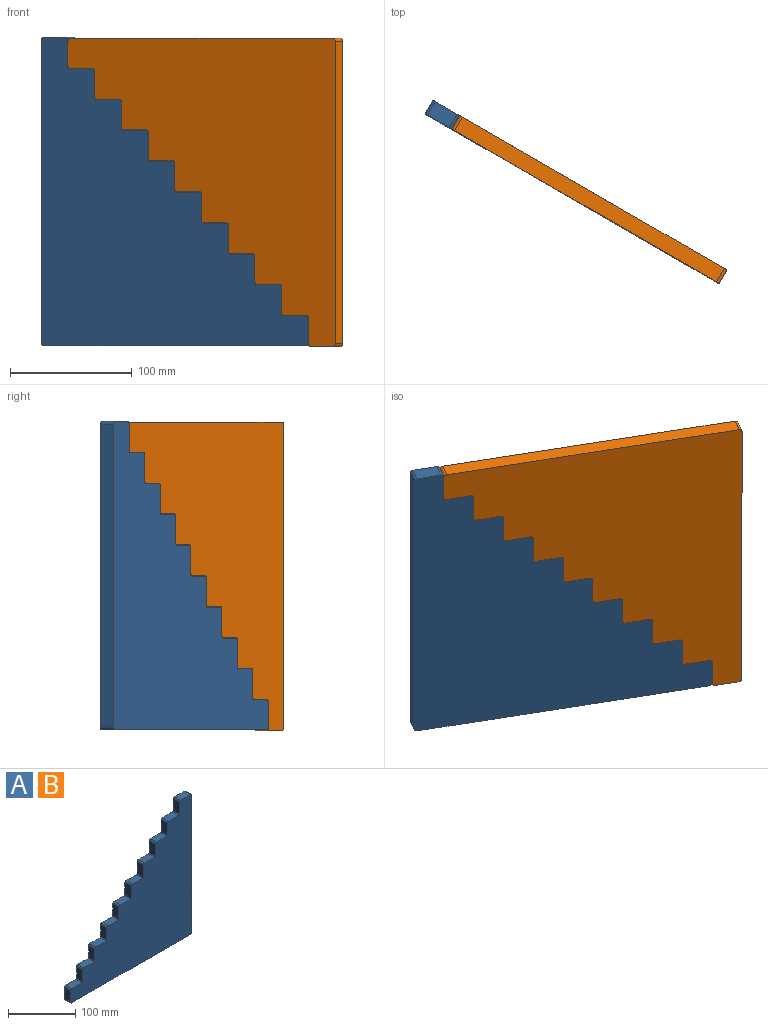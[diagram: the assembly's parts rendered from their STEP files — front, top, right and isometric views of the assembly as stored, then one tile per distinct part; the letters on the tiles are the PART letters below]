
ASSEMBLY  parts=2 mates=4
PART A: 46 faces, bbox 254x12.7x254 mm
  f0: plane 248.92x12.7mm, normal (0,0,-1), area 3161.3mm2, adj f22,f23,f24,f36
  f1: plane 248.92x12.7mm, normal (1,0,0), area 3161.3mm2, adj f22,f23,f24,f25
  f2: plane 20.32x12.7mm, normal (0,0,1), area 258.1mm2, adj f22,f23,f25,f26
  f3: plane 21.59x12.7mm, normal (-1,0,0), area 274.2mm2, adj f22,f23,f26,f37
  f4: plane 21.59x12.7mm, normal (0,0,1), area 274.2mm2, adj f22,f23,f27,f37
  f5: plane 21.59x12.7mm, normal (-1,0,0), area 274.2mm2, adj f22,f23,f27,f38
  f6: plane 21.59x12.7mm, normal (0,0,1), area 274.2mm2, adj f22,f23,f28,f38
  f7: plane 21.59x12.7mm, normal (-1,0,0), area 274.2mm2, adj f22,f23,f28,f39
  f8: plane 21.59x12.7mm, normal (0,0,1), area 274.2mm2, adj f22,f23,f29,f39
  f9: plane 21.59x12.7mm, normal (-1,0,0), area 274.2mm2, adj f22,f23,f29,f40
  f10: plane 21.59x12.7mm, normal (0,0,1), area 274.2mm2, adj f22,f23,f30,f40
  f11: plane 21.59x12.7mm, normal (-1,0,0), area 274.2mm2, adj f22,f23,f30,f41
  f12: plane 21.59x12.7mm, normal (0,0,1), area 274.2mm2, adj f22,f23,f31,f41
  f13: plane 21.59x12.7mm, normal (-1,0,0), area 274.2mm2, adj f22,f23,f31,f42
  f14: plane 21.59x12.7mm, normal (0,0,1), area 274.2mm2, adj f22,f23,f32,f42
  f15: plane 21.59x12.7mm, normal (-1,0,0), area 274.2mm2, adj f22,f23,f32,f43
  f16: plane 21.59x12.7mm, normal (0,0,1), area 274.2mm2, adj f22,f23,f33,f43
  f17: plane 21.59x12.7mm, normal (-1,0,0), area 274.2mm2, adj f22,f23,f33,f44
  f18: plane 21.59x12.7mm, normal (0,0,1), area 274.2mm2, adj f22,f23,f34,f44
  f19: plane 21.59x12.7mm, normal (-1,0,0), area 274.2mm2, adj f22,f23,f34,f45
  f20: plane 21.59x12.7mm, normal (0,0,1), area 274.2mm2, adj f22,f23,f35,f45
  f21: plane 20.32x12.7mm, normal (-1,0,0), area 258.1mm2, adj f22,f23,f35,f36
  f22: plane 254x254mm, normal (0,-1,0), area 35468.9mm2, adj f0,f1,f2,f3,f4,f5,f6,f7
  f23: plane 254x254mm, normal (0,1,0), area 35468.9mm2, adj f0,f1,f2,f3,f4,f5,f6,f7
  f24: cylinder r=2.54mm len=12.7mm, axis (0,-1,0), area 50.7mm2, adj f0,f1,f22,f23
  f25: cylinder r=2.54mm len=12.7mm, axis (0,1,0), area 50.7mm2, adj f1,f2,f22,f23
  f26: cylinder r=2.54mm len=12.7mm, axis (0,-1,0), area 50.7mm2, adj f2,f3,f22,f23
  f27: cylinder r=2.54mm len=12.7mm, axis (0,1,0), area 50.7mm2, adj f4,f5,f22,f23
  f28: cylinder r=2.54mm len=12.7mm, axis (0,1,0), area 50.7mm2, adj f6,f7,f22,f23
  f29: cylinder r=2.54mm len=12.7mm, axis (0,1,0), area 50.7mm2, adj f8,f9,f22,f23
  f30: cylinder r=2.54mm len=12.7mm, axis (0,1,0), area 50.7mm2, adj f10,f11,f22,f23
  f31: cylinder r=2.54mm len=12.7mm, axis (0,1,0), area 50.7mm2, adj f12,f13,f22,f23
  f32: cylinder r=2.54mm len=12.7mm, axis (0,1,0), area 50.7mm2, adj f14,f15,f22,f23
  f33: cylinder r=2.54mm len=12.7mm, axis (0,1,0), area 50.7mm2, adj f16,f17,f22,f23
  f34: cylinder r=2.54mm len=12.7mm, axis (0,1,0), area 50.7mm2, adj f18,f19,f22,f23
  f35: cylinder r=2.54mm len=12.7mm, axis (0,1,0), area 50.7mm2, adj f20,f21,f22,f23
  f36: cylinder r=2.54mm len=12.7mm, axis (0,1,0), area 50.7mm2, adj f0,f21,f22,f23
  f37: cylinder r=1.27mm len=12.7mm, axis (0,-1,0), area 25.3mm2, adj f3,f4,f22,f23
  f38: cylinder r=1.27mm len=12.7mm, axis (0,-1,0), area 25.3mm2, adj f5,f6,f22,f23
  f39: cylinder r=1.27mm len=12.7mm, axis (0,-1,0), area 25.3mm2, adj f7,f8,f22,f23
  f40: cylinder r=1.27mm len=12.7mm, axis (0,-1,0), area 25.3mm2, adj f9,f10,f22,f23
  f41: cylinder r=1.27mm len=12.7mm, axis (0,-1,0), area 25.3mm2, adj f11,f12,f22,f23
  f42: cylinder r=1.27mm len=12.7mm, axis (0,-1,0), area 25.3mm2, adj f13,f14,f22,f23
  f43: cylinder r=1.27mm len=12.7mm, axis (0,-1,0), area 25.3mm2, adj f15,f16,f22,f23
  f44: cylinder r=1.27mm len=12.7mm, axis (0,-1,0), area 25.3mm2, adj f17,f18,f22,f23
  f45: cylinder r=1.27mm len=12.7mm, axis (0,-1,0), area 25.3mm2, adj f19,f20,f22,f23
PART B: same geometry as A
PLACE A rot(axis=(0,0,1),150deg) t=(-282.24,93.14,152.47)mm
PLACE B rot(axis=(-0.97,0.26,0),180deg) t=(-40.27,-46.56,405.84)mm
MATE parallel B.f23 <-> A.f23  axis (-0.5,-0.87,0) through (-117.25,-2.12,316.95)mm
MATE parallel A.f20 <-> B.f2  axis (0,0,1) through (-70.64,-21.69,177.87)mm
MATE parallel B.f21 <-> A.f3  axis (-0.87,0.5,0) through (-257.06,85.94,393.14)mm
MATE parallel A.f17 <-> B.f5  axis (0.87,-0.5,0) through (-103.09,-2.96,215.34)mm
